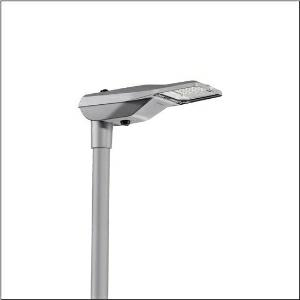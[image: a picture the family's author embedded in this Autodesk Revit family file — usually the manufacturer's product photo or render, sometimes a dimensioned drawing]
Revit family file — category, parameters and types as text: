
# Revit family: streetlight_sl_21_micro___st0_8a_5xe1c43t08db_13be
name_source: partatom
category: Lighting Fixtures
units: mm (PartAtom-declared; Revit-internal decimal feet)

## family parameters
Cut with Voids When Loaded = No
Host = Face
Light Source = No
Part Type = Normal
Room Calculation Point = No
Round Connector Dimension = Use Diameter
Shared = No

## types (1)
- --- (1 x LED, 5320 lm, 39.1 W, 4000K)
    Apparent Load = 39 VA
    CIE Flux Codes = 38 75 97 100 100
    Color Rendering = 70
    Color Temperature = 4000K
    Default Elevation = 1800 mm
    Description = Streetlight SL 21 micro, mast luminaire, primary light control with lens, of PMMA, primary optical cover: cover, of toughened safety glass, transparent, light distribution: ST0.8a, light emission: direct distribution, primary light characteristic: asymmetric, installation type: side-entry, post-top, LED, High Power LED, rated luminous flux: 5.320lm, luminous efficacy: 136lm/W, light colour: 740, colour temperature: 4000K, control gear: D4i, control: flexible luminous flux parameterisation, time-dependent luminous flux control, constant luminous flux control, overheat protection, pre-setting: logarithmic dimming characteristic, mains connection: 220..240V, AC, 50/60Hz, start of lifetime: 39W, end of service life: 41W, reduction: 18W, luminaire housing, of diecast aluminium, powder-coated, SITECO metallic grey (DB 702S), corrosivity category C5 high according to DIN EN ISO 12944, please order mast flange separately, inclination adjustable: 0°, 5°, 10°, 15°, sealing non-destructively replaceable, multi-level sealing system, length: 528mm, width: 235mm, height: 110mm, mast flange for spigot size: 42mm (side-entry): 5XC10008XM4, 60/48mm (side-entry/post-top): 5XC10108XM2, 76/60mm (side-entry/post-top): 5XC10108XM1, Smart Interface below and above, protection rating (complete): IP66, insulation class (complete): insulation class II (safety insulation), certification: CE, ENEC, ENEC+, VDE, impact resistance: IK10, permissible operating ambient temperature for outdoor applications: -40..+50°C, standard-compliant lighting for roads and squares, packaging unit: 1 piece

Light Distribution: ST0.8a
    Height = 110 mm
    Lamp = 1 x LED
    Lamp Light Flux = 5320 lm
    Lamp Power = 39.1 W
    Lamp count = 1
    Length = 528 mm
    Luminous efficacy = 136 lm/W
    Manufacturer = Siteco
    ModVariant = No
    Model = 5XE1C43T08DB
    Number of Poles = 1
    OnlyDefault = Yes
    Power Factor = 1
    Product Name = Streetlight SL 21 micro | ST0.8a
    Product group = mast luminaire | pylon top
    ProductGroupID = 6100
    Protection Class = Protection class II
    Protection Degree = IP 66
    RLX_Detail_Level = 1
    RLX_Emergency_Light_Flux = 0 lm
    RLX_Emergency_Type = 0
    RLX_Emergency_Type_DB = No
    RlxData = <blob elided: 98469 chars, md5=d412c9bf>
    Socket = socket
    Standby Power = 0 W
    System Light Flux = 5320 lm
    System Power = 39 W
    Type Comments = factory setting: luminous flux: 100 % | dim-lin: 254 | 765 mA
    Type Image = l_1007239.jpg
    URL = http://relux.com
    VarID = @adj_153805
    Voltage = 0 V
    Weight = 0.00 kg
    Width = 235 mm

## geometry (parser evidence)
native form markers: Blend x4, Sweep x10
no freeform markers — native parametric forms only
